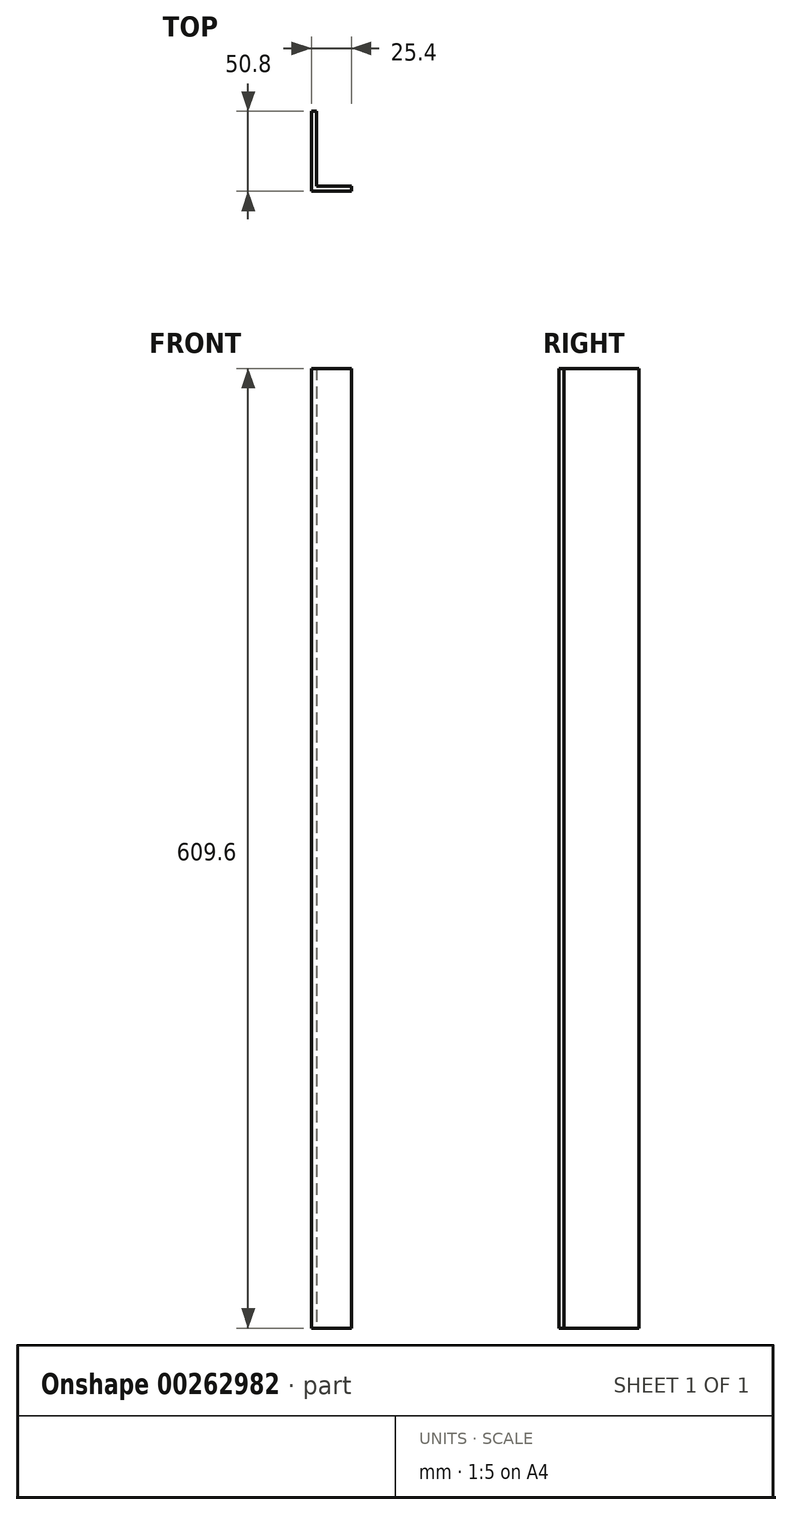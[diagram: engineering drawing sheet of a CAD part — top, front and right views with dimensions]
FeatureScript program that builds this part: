
annotation { "Feature Type Name" : "Feature", "Feature Type Description" : "" }
export const myFeature = defineFeature(function(context is Context, id is Id, definition is map)
    precondition{}
    {
        {
            var Q0;
            Q0=qCreatedBy(makeId("Top.planeOp"),FACE);
            var sketch = newSketch(context, id + "F0", { "sketchPlane" : qUnion([Q0])});
            skLineSegment(sketch, "E0", {"start": v(0, 50.8) * mm, "end": v(0, 0) * mm});
            skLineSegment(sketch, "E1", {"start": v(0, 0) * mm, "end": v(25.4, 0) * mm});
            skLineSegment(sketch, "E2", {"start": v(25.4, 0) * mm, "end": v(25.4, 3.18) * mm});
            skLineSegment(sketch, "E3", {"start": v(25.4, 3.18) * mm, "end": v(3.18, 3.17) * mm});
            skLineSegment(sketch, "E4", {"start": v(3.18, 3.17) * mm, "end": v(3.18, 50.8) * mm});
            skLineSegment(sketch, "E5", {"start": v(3.18, 50.8) * mm, "end": v(0, 50.8) * mm});
            skSolve(sketch);
        }
        {
            var Q0;
            Q0=makeQuery(id+"F0.imprint","IMPRINT",FACE,{"disambiguationData":[TD([[makeQuery(id+"F0.imprint","IMPRINT",EDGE,{"derivedFrom":sQuery(id+"F0.wireOp",EDGE,"E0")}),1.0]])]});
            extrude(context, id + "F1", {"entities" : qUnion([Q0]), "depth" : 609.6 * mm});
        }
    });
